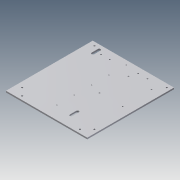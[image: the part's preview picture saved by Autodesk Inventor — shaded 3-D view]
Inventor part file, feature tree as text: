
AUTODESK INVENTOR PART (.ipt)
format: ipt  version: 2014 (Build 180170000, 170)  size: 178,176 bytes
history: native  units: mm
features: extrude x4, sketch x4
ambient origin geometry x8: Origin, YZ Plane, XZ Plane, XY Plane, X Axis, Y Axis, Z Axis, Center Point
bodies: Solid1 (feature_tree)
feature tree (8):
  extrude  "Extrusion1"  Depth=281.0mm
  extrude  "Extrusion5"  Depth=5.0mm
  extrude  "Extrusion6"  Depth=12.5mm
  extrude  "Extrusion7"  Depth=10.0mm
  sketch  "Sketch1"  dims[d0=300.0mm d1=281.0mm]
  sketch  "Sketch5"  dims[d2=5.0mm d3=0.0mm d33=18.5mm d34=18.5mm]
  sketch  "Sketch6"  dims[d35=37.5mm d36=12.5mm]
  sketch  "Sketch7"  dims[d37=5.4mm d38=12.5mm d39=37.5mm d40=43.5mm d41=10.0mm d42=0.0mm d43=250.0mm d44=15.0mm d45=60.0mm d46=3.2mm d47=6.0mm d48=25.0mm d49=40.0mm d50=10.0mm d51=0.0mm d52=50.0mm d53=51.0mm d54=25.0mm d55=54.0mm d56=50.0mm d57=30.0mm d58=4.4mm d59=10.0mm d60=27.0mm d61=37.5mm d62=22.0mm d63=9.0mm d64=3.0mm d65=60.0mm d66=3.0mm d67=15.5mm d68=31.75mm d69=42.8625mm d70=5.55625mm d71=25.003125mm d72=5.55625mm d73=4.572mm d74=35.0mm d75=40.0mm d76=100.0mm d77=80.0mm d78=4.4mm d79=20.0mm d80=20.0mm d81=10.0mm d82=0.0mm d83=12.5mm]
